# Revit family: BLAUBERG-KOMFORT_EC_DBE_900_Left
name_source: partatom
category: Mechanical Equipment
units: mm (PartAtom-declared; Revit-internal decimal feet)

## family parameters
Always vertical = Yes
Classification = None
Cut with Voids When Loaded = No
OmniClass Number = 23.75.35.14
OmniClass Title = Air Handling Units
Part Type = Normal
Room Calculation Point = No
Round Connector Dimension = Use Diameter
Shared = No
Work Plane-Based = No

## types (2) — shared parameters
B = 1351 mm  [stored 4.43241 ft]
B1 = 432 mm  [stored 1.41732 ft]
B2 = 265 mm  [stored 0.869423 ft]
Casing Material = Painted Steel Gray
Current = 17 A
D = 250 mm  [stored 0.82021 ft]
DPS_H = 198 mm  [stored 0.649606 ft]
DPS_L1 = 147 mm  [stored 0.482283 ft]
DPS_L2 = 404 mm  [stored 1.32546 ft]
Description = Air Handling Unit
Duct Connection Diameter = 250 mm  [stored 0.82021 ft]
ElBoxB = 22 mm  [stored 0.0721785 ft]
ElBoxB1 = 21 mm  [stored 0.0688976 ft]
ElBoxL = 315 mm  [stored 1.03346 ft]
Extract Air Filter = G4
Family Version = 1.0
Front Maintenance Zone Height = 800 mm  [stored 2.62467 ft]
Front Maintenance Zone Length = 1349 mm  [stored 4.42585 ft]
Front Maintenance Zone Width = 318 mm  [stored 1.04331 ft]
H = 318 mm  [stored 1.04331 ft]
H1 = 143 mm
HDrainCon = 31 mm  [stored 0.101706 ft]
Heat Exchanger Type = counter-flow
Heater power = 3300 W
L = 1349 mm  [stored 4.42585 ft]
LDrainCon = 28 mm  [stored 0.0918635 ft]
LDrainCon1 = 435 mm  [stored 1.42717 ft]
LDrainCon2 = 582 mm  [stored 1.90945 ft]
LDuctCon = 50 mm  [stored 0.164042 ft]
Load Classification = HVAC
Maintenance Zone Material = Maintenance Zone
Manufacturer = Blauberg
Maximum Air Flow = 1030 m³/h
Maximum Unit Current With Electric Heater = 17 A
Maximum Unit Current Without Electric Heater = 3 A
Maximum Unit Power Without Electric Heater = 442 W
Metal Material = Metal Zinc
Number of Poles = 1
Power = 3742 W
Power Factor = 1
RPM (min-1) = 2720
SEC Class = A
Sound Pressure Level at 3 m (dBA) = 33
Supply Air Filter = G4 (F7 option)
Transported Air Temperature (°C) = -25…+40
URL = https://blaubergventilatoren.de
Voltage = 230 V
Weight = 111.00 kg

## per-type parameters (varying)
| type | Drain Connection Diameter | DrainD | DrainPipe | Heat Exchanger Material | Heat recovery efficiency (%) | Type Comments |
| KOMFORT EC DBE 900 L S21 | 14 mm  [stored 0.0459318 ft] | 14 mm  [stored 0.0459318 ft] | Yes | polystyrene | 75..88 | Air Handling Unit KOMFORT EC DBE 900 L S21 |
| KOMFORT EC DBE 900-E L S21 | 0 mm  [stored 0 ft] | 1 mm  [stored 0.00328084 ft] | No | enthalpy | 69..85 | Air Handling Unit KOMFORT EC DBE 900-E L S21 |

note: column(s) folded — value = type name in every type: Model

note: [stored X ft] marks values corroborated as IEEE doubles in the binary element streams (Revit-internal decimal feet)

## geometry (parser evidence)
native form markers: Sweep x5
no freeform markers — native parametric forms only
